# Revit family: Keilmutter für Verbunddecken
name_source: partatom
category: HLS-Bauteile
revit_build: Autodesk Revit 2017 (Build: 20190507_1515(x64)
units: mm (PartAtom-declared; Revit-internal decimal feet)

## family parameters
Arbeitsebenenbasiert = Ja
Beim Laden mit Abzugskörper schneiden = Nein
Bemaßung runder Anschluss = Durchmesser verwenden
Gemeinsam genutzt = Ja
Immer vertikal = Nein
Raumberechnungspunkt = Nein
Teiletyp = Normal

## types (2) — shared parameters
Fabrikat = MEFA
Firma = MEFA Befestigungs- und Montagesysteme GmbH
Gewicht = 0.02 kg
Gewicht pro Bauteil = 0.02 kg
Kurztext1 = Keilmutter Verbunddecke
Material = Stahl
Mengeneinheit = St
Vorgabe-Ansicht = 1219 mm
vpe = 100 St

## per-type parameters (varying)
| type | Artikelnummer | D | EAN | Kurztext2 |
| Keilmutter mit IG M 8 | 0819715 | 7 mm  [stored 0.0229659 ft] | 4250928420695 | M8 25 x 12,5 mm gvz |
| Keilmutter mit IG M10 | 0819722 | 9 mm  [stored 0.0295276 ft] | 4250928420701 | M10 25 x 12,5 mm gvz |

note: [stored X ft] marks values corroborated as IEEE doubles in the binary element streams (Revit-internal decimal feet)
